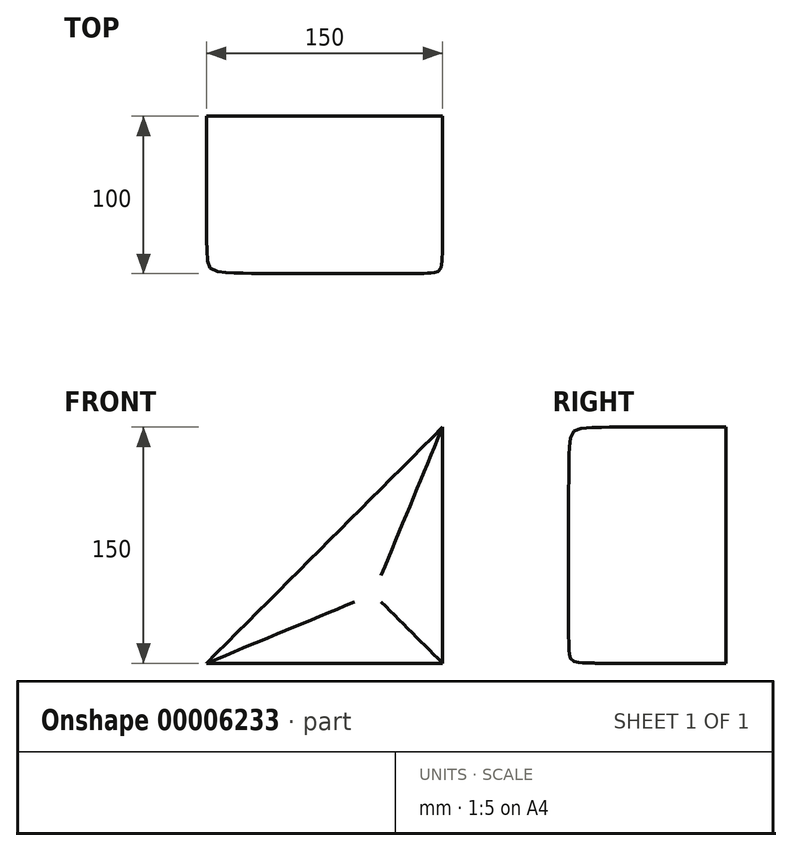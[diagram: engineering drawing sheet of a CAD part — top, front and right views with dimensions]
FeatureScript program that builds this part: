
annotation { "Feature Type Name" : "Feature", "Feature Type Description" : "" }
export const myFeature = defineFeature(function(context is Context, id is Id, definition is map)
    precondition{}
    {
        {
            var Q0;
            Q0=qCreatedBy(makeId("Front.planeOp"),FACE);
            var sketch = newSketch(context, id + "F0", { "sketchPlane" : qUnion([Q0])});
            skLineSegment(sketch, "E0.rect.bottom", {"start": v(75, -75) * mm, "end": v(-75, -75) * mm, "construction": true});
            skLineSegment(sketch, "E0.rect.top", {"start": v(75, 75) * mm, "end": v(-75, 75) * mm, "construction": true});
            skLineSegment(sketch, "E0.rect.left", {"start": v(75, -75) * mm, "end": v(75, 75) * mm, "construction": true});
            skLineSegment(sketch, "E0.rect.right", {"start": v(-75, -75) * mm, "end": v(-75, 75) * mm, "construction": true});
            skPoint(sketch, "E0.rect.middle", {"position": v(0, 0) * mm});
            skLineSegment(sketch, "E1", {"start": v(-75, -75) * mm, "end": v(75, -75) * mm});
            skLineSegment(sketch, "E2", {"start": v(75, 75) * mm, "end": v(-75, -75) * mm});
            skLineSegment(sketch, "E3", {"start": v(75, 75) * mm, "end": v(75, -75) * mm});
            skSolve(sketch);
        }
        {
            var Q0;
            Q0=makeQuery(id+"F0.imprint","IMPRINT",FACE,{"disambiguationData":[TD([[makeQuery(id+"F0.imprint","IMPRINT",EDGE,{"derivedFrom":sQuery(id+"F0.wireOp",EDGE,"E1")}),1.0]])]});
            extrude(context, id + "F1", {"entities" : qUnion([Q0]), "depth" : 100 * mm});
        }
        {
            var Q0;
            Q0=makeQuery(id+"F1.opExtrude","CAP_EDGE",EDGE,{"disambiguationData":[OSD([sQuery(id+"F0.wireOp",EDGE,"8e4ecb72-4ed7-4ffe-99f2-073ee20e7a5f.2")])],"isStart":false});
            var Q1;
            Q1=makeQuery(id+"F1.opExtrude","CAP_EDGE",EDGE,{"disambiguationData":[OSD([sQuery(id+"F0.wireOp",EDGE,"8e4ecb72-4ed7-4ffe-99f2-073ee20e7a5f.1")])],"isStart":false});
            var Q2;
            Q2=makeQuery(id+"F1.opExtrude","CAP_EDGE",EDGE,{"disambiguationData":[OSD([sQuery(id+"F0.wireOp",EDGE,"8e4ecb72-4ed7-4ffe-99f2-073ee20e7a5f.0")])],"isStart":false});
            var Q3;
            Q3=makeQuery(id+"F1.opExtrude","CAP_FACE",FACE,{"disambiguationData":[OSD([sQuery(id+"F0.wireOp",EDGE,"E1"),sQuery(id+"F0.wireOp",EDGE,"E2"),sQuery(id+"F0.wireOp",EDGE,"E3")])],"isStart":false});
            fillet(context, id + "F2", {"entities" : qUnion([Q0, Q1, Q2, Q3]), "radius" : 39 * mm, "tangentPropagation" : true, "rho" : 0.9, "crossSection" : FilletCrossSection.CONIC, "allowEdgeOverflow" : false});
        }
    });
